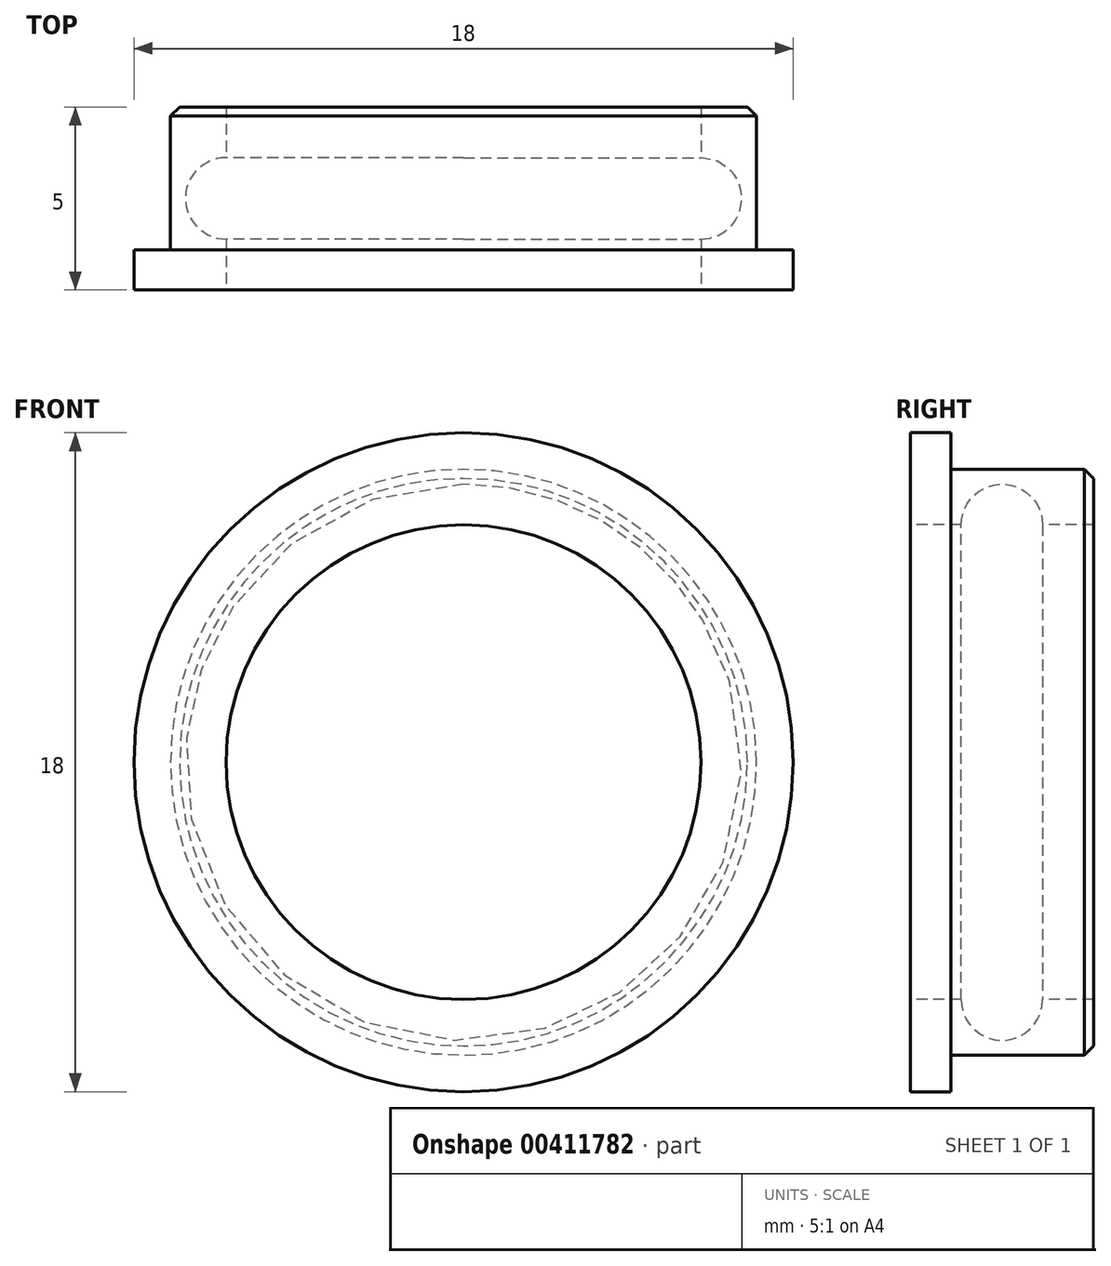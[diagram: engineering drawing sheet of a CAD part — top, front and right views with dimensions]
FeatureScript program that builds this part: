
annotation { "Feature Type Name" : "Feature", "Feature Type Description" : "" }
export const myFeature = defineFeature(function(context is Context, id is Id, definition is map)
    precondition{}
    {
        {
            var Q0;
            Q0=qCreatedBy(makeId("Front.planeOp"),FACE);
            var sketch = newSketch(context, id + "F0", { "sketchPlane" : qUnion([Q0])});
            skCircle(sketch, "E0", {"center": v(0, 0) * mm, "radius": 9 * mm});
            skCircle(sketch, "E1", {"center": v(0, 0) * mm, "radius": 6.48 * mm});
            skSolve(sketch);
        }
        {
            var Q0;
            Q0=qSketchRegion(id+"F0",true);
            extrude(context, id + "F1", {"entities" : qUnion([Q0]), "oppositeDirection" : true, "depth" : 1.1 * mm});
        }
        {
            var Q0;
            Q0=makeQuery(id+"F1.opExtrude","CAP_FACE",FACE,{"disambiguationData":[OSD([sQuery(id+"F0.wireOp",EDGE,"E0"),sQuery(id+"F0.wireOp",EDGE,"E1")])],"isStart":false});
            var sketch = newSketch(context, id + "F2", { "sketchPlane" : qUnion([Q0])});
            skCircle(sketch, "E2", {"center": v(0, 0) * mm, "radius": 8 * mm});
            skSolve(sketch);
        }
        {
            var Q0;
            Q0=makeQuery(id+"F2.imprint","IMPRINT",FACE,{"disambiguationData":[TD([[makeQuery(id+"F2.imprint","IMPRINT",EDGE,{"derivedFrom":sQuery(id+"F2.wireOp",EDGE,"E2")}),1.0]])]});
            extrude(context, id + "F3", {"entities" : qUnion([Q0]), "operationType" : NewBodyOperationType.ADD, "depth" : 3.65 * mm});
        }
        {
            var Q0;
            Q0=makeQuery(id+"F3.opExtrude","CAP_FACE",FACE,{"disambiguationData":[OSD([sQuery(id+"F0.wireOp",EDGE,"E1"),sQuery(id+"F2.wireOp",EDGE,"E2")])],"isStart":false});
            extrude(context, id + "F4", {"entities" : qUnion([Q0]), "operationType" : NewBodyOperationType.ADD, "depth" : 0.25 * mm});
        }
        {
            var Q0;
            Q0=makeQuery(id+"F4.opExtrude","CAP_EDGE",EDGE,{"disambiguationData":[OSD([sQuery(id+"F2.wireOp",EDGE,"E2")])],"isStart":false});
            chamfer(context, id + "F5", {"entities" : qUnion([Q0]), "width" : 0.25 * mm, "tangentPropagation" : true});
        }
        {
            var Q0;
            Q0=makeQuery(id+"F1.opExtrude","CAP_FACE",FACE,{"disambiguationData":[OSD([sQuery(id+"F0.wireOp",EDGE,"E0"),sQuery(id+"F0.wireOp",EDGE,"E1")])],"isStart":true});
            cPlane(context, id + "F6", {"entities" : qUnion([Q0]), "cplaneType" : CPlaneType.OFFSET, "offset" : 1.39 * mm, "oppositeDirection" : true, "width" : 150 * mm, "height" : 150 * mm});
        }
        {
            var Q0;
            Q0=qCreatedBy(id+"F6.planeOp",FACE);
            var sketch = newSketch(context, id + "F7", { "sketchPlane" : qUnion([Q0])});
            skCircle(sketch, "E3.0", {"center": v(0, 0) * mm, "radius": 6.48 * mm});
            skSolve(sketch);
        }
        {
            var Q0;
            Q0=makeQuery(id+"F1.opExtrude","CAP_EDGE",EDGE,{"disambiguationData":[OSD([sQuery(id+"F0.wireOp",EDGE,"E1")])],"isStart":true});
            cPlane(context, id + "F8", {"entities" : qUnion([Q0]), "cplaneType" : CPlaneType.LINE_ANGLE, "offset" : 25 * mm, "angle" : 90 * degree, "width" : 150 * mm, "height" : 150 * mm});
        }
        {
            var Q0;
            Q0=qCreatedBy(id+"F8.planeOp",FACE);
            var sketch = newSketch(context, id + "F9", { "sketchPlane" : qUnion([Q0])});
            skLineSegment(sketch, "E4.0.0", {"start": v(1.39, -6.48) * mm, "end": v(1.39, 6.48) * mm});
            skArc(sketch, "E5", {"start": v(3.61, 6.48) * mm, "mid": v(2.5, 7.6) * mm, "end": v(1.39, 6.48) * mm});
            skLineSegment(sketch, "E6", {"start": v(1.39, 6.48) * mm, "end": v(3.61, 6.48) * mm});
            skLineSegment(sketch, "E7", {"start": v(-6.73, 0) * mm, "end": v(11.07, 0) * mm, "construction": true});
            skSolve(sketch);
        }
        {
            var Q0;
            Q0=qSketchRegion(id+"F9",true);
            var Q1;
            Q1=sQuery(id+"F9.wireOp",EDGE,"E7");
            revolve(context, id + "F10", {"operationType" : NewBodyOperationType.REMOVE, "entities" : qUnion([Q0]), "axis" : qUnion([Q1]), "revolveType" : RevolveType.FULL, "oppositeDirection" : true});
        }
    });
